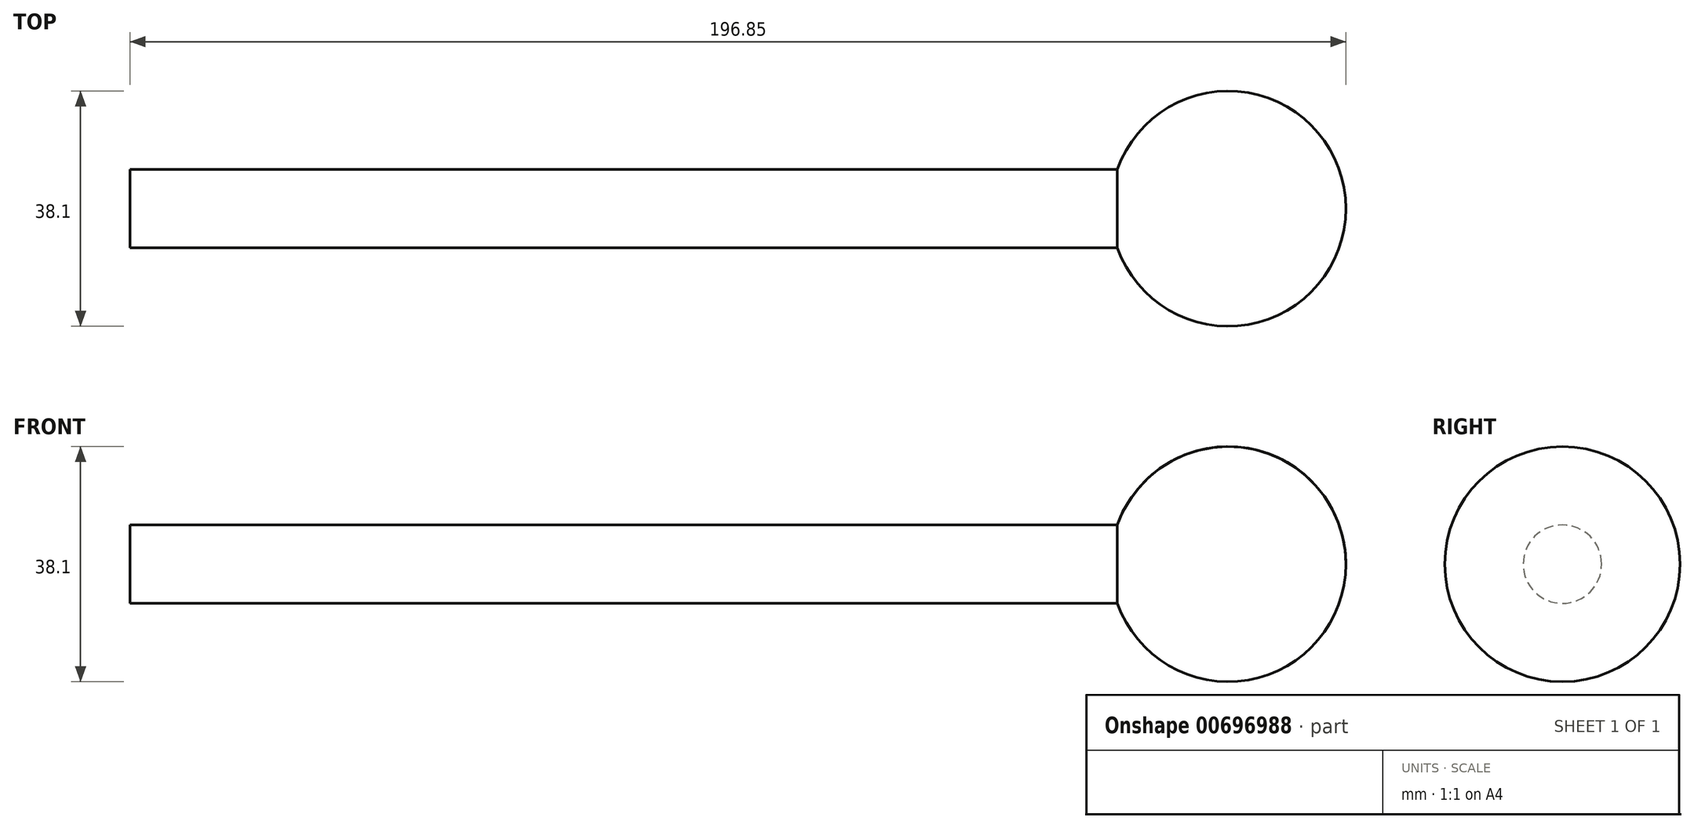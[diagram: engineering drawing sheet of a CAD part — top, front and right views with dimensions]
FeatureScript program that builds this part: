
annotation { "Feature Type Name" : "Feature", "Feature Type Description" : "" }
export const myFeature = defineFeature(function(context is Context, id is Id, definition is map)
    precondition{}
    {
        {
            var Q0;
            Q0=qCreatedBy(makeId("Front.planeOp"),FACE);
            var sketch = newSketch(context, id + "F0", { "sketchPlane" : qUnion([Q0])});
            skLineSegment(sketch, "E0", {"start": v(-88.9, 0) * mm, "end": v(-88.9, 6.35) * mm});
            skLineSegment(sketch, "E1", {"start": v(-88.9, 6.35) * mm, "end": v(70.94, 6.35) * mm});
            skArc(sketch, "E2", {"start": v(107.95, 0) * mm, "mid": v(92.12, 18.78) * mm, "end": v(70.94, 6.35) * mm});
            skLineSegment(sketch, "E3", {"start": v(-88.9, 0) * mm, "end": v(69.85, 0) * mm});
            skLineSegment(sketch, "E4", {"start": v(69.85, 0) * mm, "end": v(107.95, 0) * mm});
            skSolve(sketch);
        }
        {
            var Q0;
            Q0=makeQuery(id+"F0.imprint","IMPRINT",FACE,{"disambiguationData":[TD([[makeQuery(id+"F0.imprint","IMPRINT",EDGE,{"derivedFrom":sQuery(id+"F0.wireOp",EDGE,"E0")}),-1.0]])]});
            var Q1;
            Q1=sQuery(id+"F0.wireOp",EDGE,"E3");
            revolve(context, id + "F1", {"entities" : qUnion([Q0]), "axis" : qUnion([Q1]), "revolveType" : RevolveType.FULL});
        }
    });
